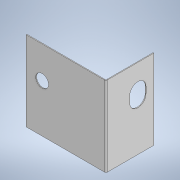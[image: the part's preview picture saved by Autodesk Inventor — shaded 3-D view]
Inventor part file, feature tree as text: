
AUTODESK INVENTOR PART (.ipt)
format: ipt  version: 2022 (Build 260153000, 153)  size: 138,752 bytes
history: native  units: mm
features: sheet_metal_op x3, sketch x3, extrude x2, other x1
ambient origin geometry x8: Origin, YZ Plane, XZ Plane, XY Plane, X Axis, Y Axis, Z Axis, Center Point
bodies: Solid1 (feature_tree)
feature tree (9):
  sheet_metal_op  "Contour Flange1"
  extrude  "Extrusion1"  Depth=50.0mm
  extrude  "Extrusion2"  Depth=0.5mm
  sketch  "Sketch1"  dims[d0=30.0mm d1=50.0mm]
  other  "Plate1"
  sheet_metal_op  "Bend1"
  sheet_metal_op  "Corner1"
  sketch  "Sketch2"  dims[d2=0.5mm d3=0.5mm]
  sketch  "Sketch3"  dims[d4=0.25mm d5=1.0mm d6=0.5mm d7=50.0mm d8=0.5mm d9=0.5mm d10=2.0mm d11=0.5mm d12=0.5mm d13=10.2mm d14=10.2mm d16=10.0mm d17=4.0mm d18=2.0mm d19=10.0mm d20=0.0mm d21=40.0mm d22=8.0mm d24=10.0mm d25=0.0mm d26=17.5mm d27=20.0mm]
